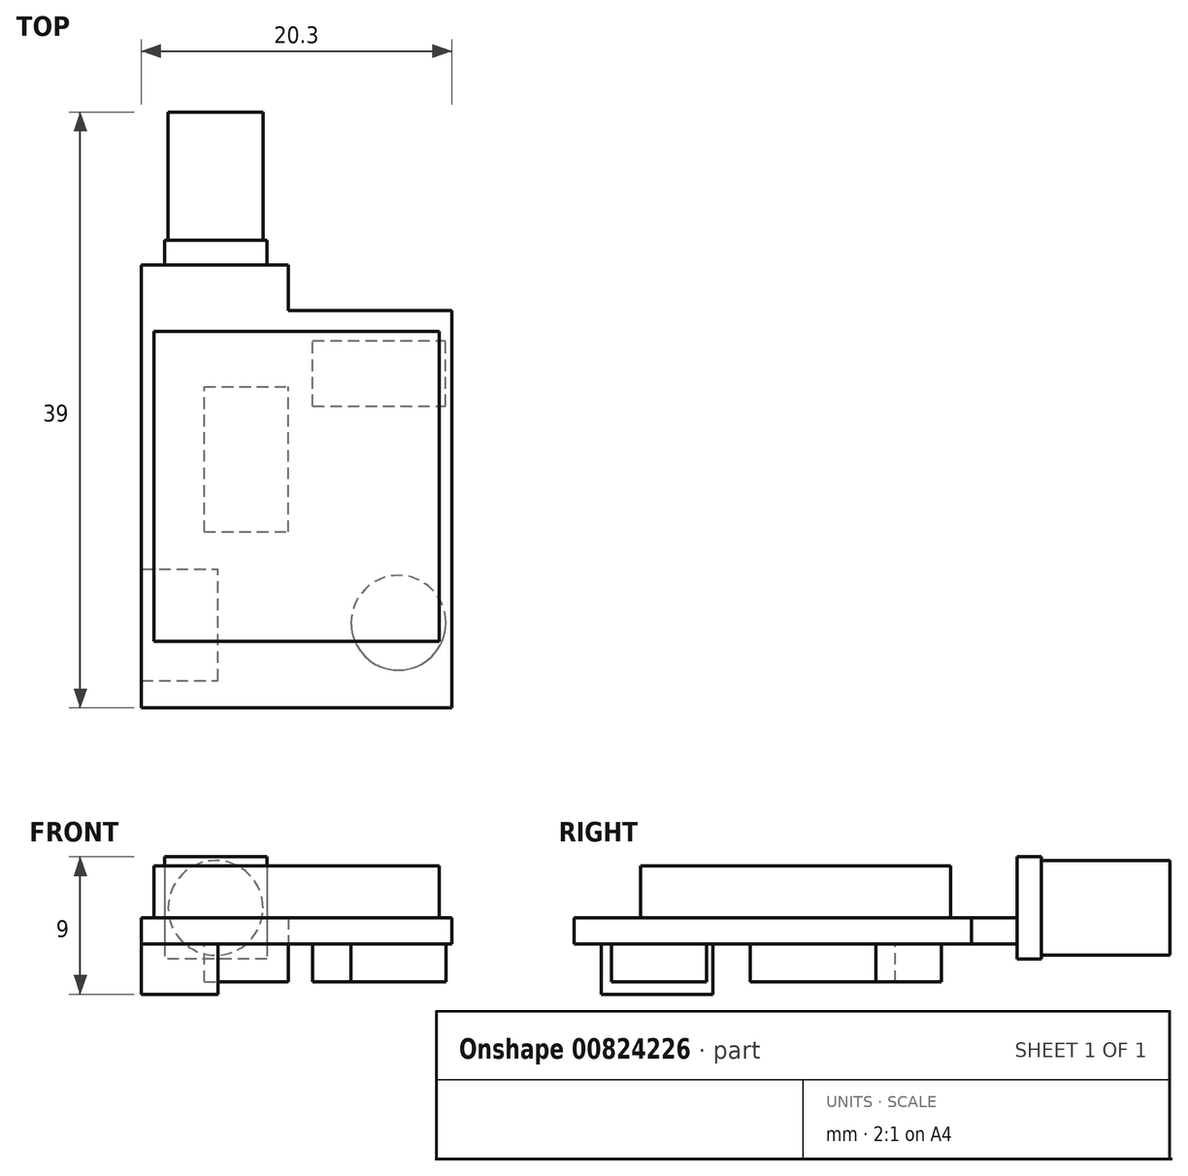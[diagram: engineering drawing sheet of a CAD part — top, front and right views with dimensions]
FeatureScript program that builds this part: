
annotation { "Feature Type Name" : "Feature", "Feature Type Description" : "" }
export const myFeature = defineFeature(function(context is Context, id is Id, definition is map)
    precondition{}
    {
        {
            var Q0;
            Q0=qCreatedBy(makeId("Top.planeOp"),FACE);
            var sketch = newSketch(context, id + "F0", { "sketchPlane" : qUnion([Q0])});
            skLineSegment(sketch, "E0.bottom", {"start": v(10.15, -14.5) * mm, "end": v(-10.15, -14.5) * mm});
            skLineSegment(sketch, "E0.top", {"start": v(10.15, 14.5) * mm, "end": v(-10.15, 14.5) * mm});
            skLineSegment(sketch, "E0.left", {"start": v(10.15, -14.5) * mm, "end": v(10.15, 14.5) * mm});
            skLineSegment(sketch, "E0.right", {"start": v(-10.15, -14.5) * mm, "end": v(-10.15, 14.5) * mm});
            skPoint(sketch, "E0.middle", {"position": v(0, 0) * mm});
            skLineSegment(sketch, "E1.bottom", {"start": v(10.15, 14.5) * mm, "end": v(-0.55, 14.5) * mm});
            skLineSegment(sketch, "E1.top", {"start": v(10.15, 11.5) * mm, "end": v(-0.55, 11.5) * mm});
            skLineSegment(sketch, "E1.left", {"start": v(10.15, 14.5) * mm, "end": v(10.15, 11.5) * mm});
            skLineSegment(sketch, "E1.right", {"start": v(-0.55, 14.5) * mm, "end": v(-0.55, 11.5) * mm});
            skSolve(sketch);
        }
        {
            var Q0;
            Q0=makeQuery(id+"F0.imprint","IMPRINT",FACE,{"disambiguationData":[TD([[makeQuery(id+"F0.imprint","IMPRINT",EDGE,{"derivedFrom":sQuery(id+"F0.wireOp",EDGE,"E0.bottom")}),-1.0]])]});
            extrude(context, id + "F1", {"entities" : qUnion([Q0]), "depth" : 1.7 * mm, "offsetDistance" : 25 * mm});
        }
        {
            var Q0;
            Q0=makeQuery(id+"F1.opExtrude","CAP_FACE",FACE,{"disambiguationData":[OSD([sQuery(id+"F0.wireOp",EDGE,"E0.bottom"),sQuery(id+"F0.wireOp",EDGE,"E0.top"),sQuery(id+"F0.wireOp",EDGE,"E0.left"),sQuery(id+"F0.wireOp",EDGE,"E0.right")])],"isStart":false});
            var sketch = newSketch(context, id + "F2", { "sketchPlane" : qUnion([Q0])});
            skLineSegment(sketch, "E2.bottom", {"start": v(9.35, -10.15) * mm, "end": v(-9.35, -10.15) * mm});
            skLineSegment(sketch, "E2.top", {"start": v(9.35, 10.15) * mm, "end": v(-9.35, 10.15) * mm});
            skLineSegment(sketch, "E2.left", {"start": v(9.35, -10.15) * mm, "end": v(9.35, 10.15) * mm});
            skLineSegment(sketch, "E2.right", {"start": v(-9.35, -10.15) * mm, "end": v(-9.35, 10.15) * mm});
            skPoint(sketch, "E2.middle", {"position": v(0, 0) * mm});
            skSolve(sketch);
        }
        {
            var Q0;
            Q0=makeQuery(id+"F2.imprint","IMPRINT",FACE,{"disambiguationData":[TD([[makeQuery(id+"F2.imprint","IMPRINT",EDGE,{"derivedFrom":sQuery(id+"F2.wireOp",EDGE,"E2.bottom")}),-1.0]])]});
            extrude(context, id + "F3", {"entities" : qUnion([Q0]), "operationType" : NewBodyOperationType.ADD, "depth" : 3.4 * mm, "offsetDistance" : 25 * mm});
        }
        {
            var Q0;
            Q0=makeQuery(id+"F1.opExtrude","CAP_FACE",FACE,{"disambiguationData":[OSD([sQuery(id+"F0.wireOp",EDGE,"E0.bottom"),sQuery(id+"F0.wireOp",EDGE,"E0.top"),sQuery(id+"F0.wireOp",EDGE,"E0.left"),sQuery(id+"F0.wireOp",EDGE,"E0.right"),sQuery(id+"F0.wireOp",EDGE,"E1.top"),sQuery(id+"F0.wireOp",EDGE,"E1.right")])],"isStart":true});
            var sketch = newSketch(context, id + "F4", { "sketchPlane" : qUnion([Q0])});
            skLineSegment(sketch, "E3.bottom", {"start": v(-10.15, 12.7) * mm, "end": v(-5.15, 12.7) * mm});
            skLineSegment(sketch, "E3.top", {"start": v(-10.15, 5.4) * mm, "end": v(-5.15, 5.4) * mm});
            skLineSegment(sketch, "E3.left", {"start": v(-10.15, 12.7) * mm, "end": v(-10.15, 5.4) * mm});
            skLineSegment(sketch, "E3.right", {"start": v(-5.15, 12.7) * mm, "end": v(-5.15, 5.4) * mm});
            skLineSegment(sketch, "E4.bottom", {"start": v(-6.04, 2.98) * mm, "end": v(-0.54, 2.98) * mm});
            skLineSegment(sketch, "E4.top", {"start": v(-6.04, -6.52) * mm, "end": v(-0.54, -6.52) * mm});
            skLineSegment(sketch, "E4.left", {"start": v(-6.04, 2.98) * mm, "end": v(-6.04, -6.52) * mm});
            skLineSegment(sketch, "E4.right", {"start": v(-0.54, 2.98) * mm, "end": v(-0.54, -6.52) * mm});
            skLineSegment(sketch, "E5.bottom", {"start": v(1.06, -5.25) * mm, "end": v(9.76, -5.25) * mm});
            skLineSegment(sketch, "E5.top", {"start": v(1.06, -9.55) * mm, "end": v(9.76, -9.55) * mm});
            skLineSegment(sketch, "E5.left", {"start": v(1.06, -5.25) * mm, "end": v(1.06, -9.55) * mm});
            skLineSegment(sketch, "E5.right", {"start": v(9.76, -5.25) * mm, "end": v(9.76, -9.55) * mm});
            skCircle(sketch, "E6", {"center": v(6.66, 8.93) * mm, "radius": 3.1 * mm});
            skSolve(sketch);
        }
        {
            var Q0;
            Q0=makeQuery(id+"F4.imprint","IMPRINT",FACE,{"disambiguationData":[TD([[makeQuery(id+"F4.imprint","IMPRINT",EDGE,{"derivedFrom":sQuery(id+"F4.wireOp",EDGE,"E3.bottom")}),-1.0]])]});
            extrude(context, id + "F5", {"entities" : qUnion([Q0]), "operationType" : NewBodyOperationType.ADD, "depth" : 3.3 * mm, "offsetDistance" : 25 * mm});
        }
        {
            var Q0;
            Q0=makeQuery(id+"F4.imprint","IMPRINT",FACE,{"disambiguationData":[TD([[makeQuery(id+"F4.imprint","IMPRINT",EDGE,{"derivedFrom":sQuery(id+"F4.wireOp",EDGE,"E4.bottom")}),-1.0]])]});
            var Q1;
            Q1=makeQuery(id+"F4.imprint","IMPRINT",FACE,{"disambiguationData":[TD([[makeQuery(id+"F4.imprint","IMPRINT",EDGE,{"derivedFrom":sQuery(id+"F4.wireOp",EDGE,"E5.bottom")}),-1.0]])]});
            var Q2;
            Q2=makeQuery(id+"F4.imprint","IMPRINT",FACE,{"disambiguationData":[TD([[makeQuery(id+"F4.imprint","IMPRINT",EDGE,{"derivedFrom":sQuery(id+"F4.wireOp",EDGE,"E6")}),1.0]])]});
            extrude(context, id + "F6", {"entities" : qUnion([Q0, Q1, Q2]), "operationType" : NewBodyOperationType.ADD, "depth" : 2.5 * mm, "offsetDistance" : 25 * mm});
        }
        {
            var Q0;
            Q0=makeQuery(id+"F1.opExtrude","SWEPT_FACE",FACE,{"disambiguationData":[OSD([sQuery(id+"F0.wireOp",EDGE,"E0.top")])]});
            var sketch = newSketch(context, id + "F7", { "sketchPlane" : qUnion([Q0])});
            skLineSegment(sketch, "E7.bottom", {"start": v(1.95, 5.7) * mm, "end": v(8.65, 5.7) * mm});
            skLineSegment(sketch, "E7.top", {"start": v(1.95, -1) * mm, "end": v(8.65, -1) * mm});
            skLineSegment(sketch, "E7.left", {"start": v(1.95, 5.7) * mm, "end": v(1.95, -1) * mm});
            skLineSegment(sketch, "E7.right", {"start": v(8.65, 5.7) * mm, "end": v(8.65, -1) * mm});
            skSolve(sketch);
        }
        {
            var Q0;
            Q0 = qSketchRegion(id + "F7", true);
            extrude(context, id + "F8", {"entities" : qUnion([Q0]), "operationType" : NewBodyOperationType.ADD, "depth" : 1.6 * mm, "offsetDistance" : 25 * mm});
        }
        {
            var Q0;
            Q0=makeQuery(id+"F8.opExtrude","CAP_FACE",FACE,{"disambiguationData":[OSD([sQuery(id+"F7.wireOp",EDGE,"E7.bottom"),sQuery(id+"F7.wireOp",EDGE,"E7.top"),sQuery(id+"F7.wireOp",EDGE,"E7.left"),sQuery(id+"F7.wireOp",EDGE,"E7.right")])],"isStart":false});
            var sketch = newSketch(context, id + "F9", { "sketchPlane" : qUnion([Q0])});
            skCircle(sketch, "E8", {"center": v(5.3, 2.35) * mm, "radius": 3.1 * mm});
            skPoint(sketch, "E8.centerSnap0", {"position": v(5.3, 5.7) * mm});
            skPoint(sketch, "E8.centerSnap1", {"position": v(1.95, 2.35) * mm});
            skSolve(sketch);
        }
        {
            var Q0;
            Q0=makeQuery(id+"F9.imprint","IMPRINT",FACE,{"disambiguationData":[TD([[makeQuery(id+"F9.imprint","IMPRINT",EDGE,{"derivedFrom":sQuery(id+"F9.wireOp",EDGE,"E8")}),1.0]])]});
            extrude(context, id + "F10", {"entities" : qUnion([Q0]), "operationType" : NewBodyOperationType.ADD, "depth" : (39 - 30.6) * mm, "offsetDistance" : 25 * mm});
        }
    });
